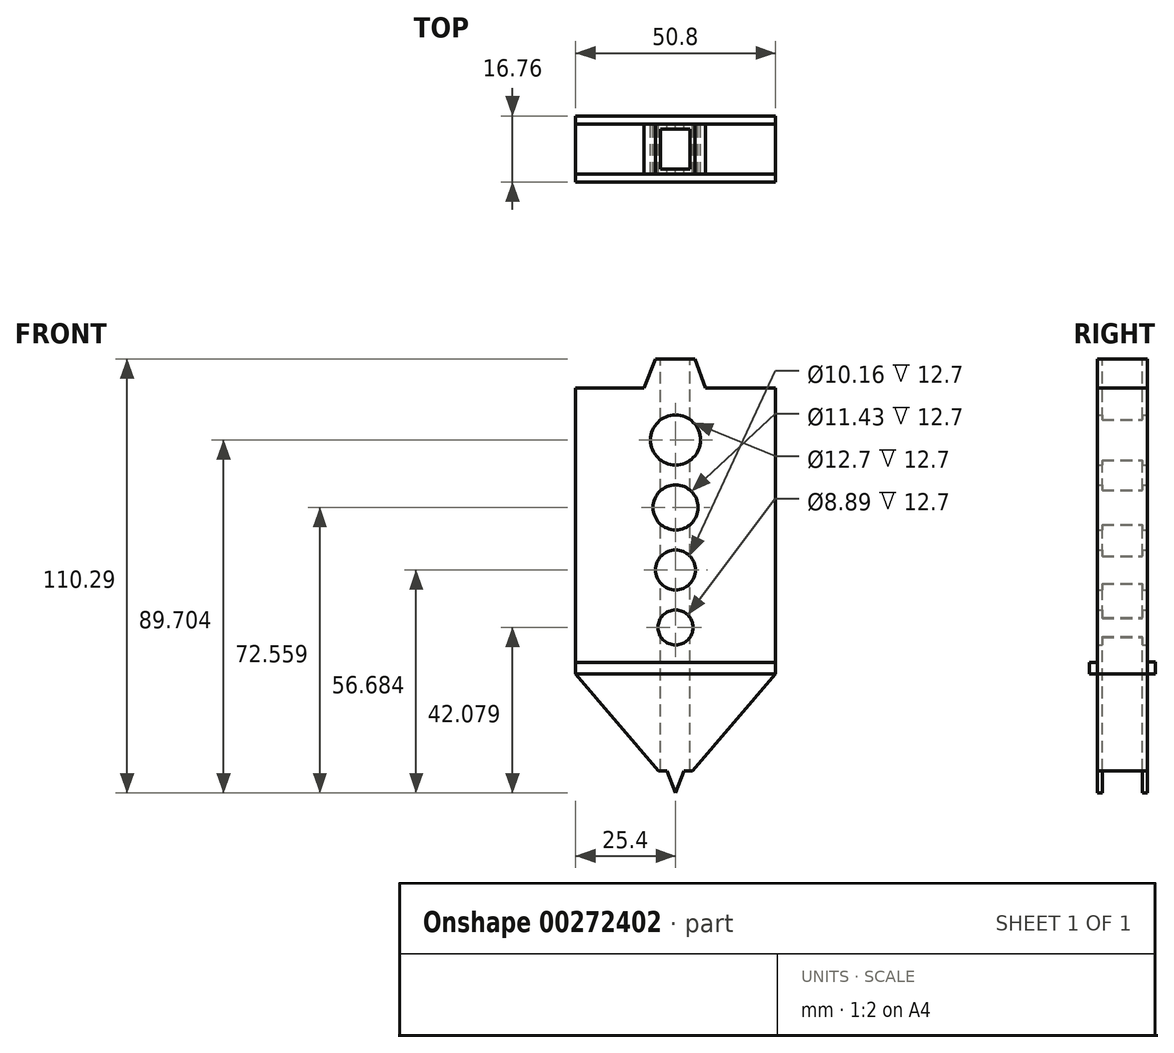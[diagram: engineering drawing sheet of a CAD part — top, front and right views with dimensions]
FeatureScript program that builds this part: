
annotation { "Feature Type Name" : "Feature", "Feature Type Description" : "" }
export const myFeature = defineFeature(function(context is Context, id is Id, definition is map)
    precondition{}
    {
        {
            var Q0;
            Q0=qCreatedBy(makeId("Front.planeOp"),FACE);
            var sketch = newSketch(context, id + "F0", { "sketchPlane" : qUnion([Q0])});
            skLineSegment(sketch, "E0", {"start": v(0, 0) * mm, "end": v(-25.4, 0) * mm});
            skLineSegment(sketch, "E1", {"start": v(0, 0) * mm, "end": v(25.4, 0) * mm});
            skLineSegment(sketch, "E2", {"start": v(-25.4, 0) * mm, "end": v(-4.32, -24.62) * mm});
            skLineSegment(sketch, "E3", {"start": v(-4.32, -24.62) * mm, "end": v(0, -24.62) * mm});
            skLineSegment(sketch, "E4", {"start": v(0, -24.62) * mm, "end": v(4.32, -24.62) * mm});
            skLineSegment(sketch, "E5", {"start": v(4.32, -24.62) * mm, "end": v(25.4, 0) * mm});
            skLineSegment(sketch, "E6", {"start": v(-2.16, -24.62) * mm, "end": v(0, -30.28) * mm});
            skLineSegment(sketch, "E7", {"start": v(0, -30.28) * mm, "end": v(2.16, -24.62) * mm});
            skLineSegment(sketch, "E8", {"start": v(-25.4, 0) * mm, "end": v(-25.4, 72.62) * mm});
            skLineSegment(sketch, "E9", {"start": v(-25.4, 72.62) * mm, "end": v(25.4, 72.62) * mm});
            skLineSegment(sketch, "E10", {"start": v(25.4, 72.62) * mm, "end": v(25.4, 0) * mm});
            skLineSegment(sketch, "E11", {"start": v(-8, 72.62) * mm, "end": v(-5.05, 80.01) * mm});
            skLineSegment(sketch, "E12", {"start": v(-5.05, 80.01) * mm, "end": v(4.91, 80.01) * mm});
            skLineSegment(sketch, "E13", {"start": v(4.91, 80.01) * mm, "end": v(7.55, 72.62) * mm});
            skLineSegment(sketch, "E14", {"start": v(0, 80.01) * mm, "end": v(-0.07, 72.62) * mm});
            skPoint(sketch, "E14.endSnap0", {"position": v(-0.07, 80.01) * mm});
            skCircle(sketch, "E15", {"center": v(0, 59.42) * mm, "radius": 6.35 * mm});
            skCircle(sketch, "E16", {"center": v(0, 42.28) * mm, "radius": 5.72 * mm});
            skCircle(sketch, "E17", {"center": v(0, 26.4) * mm, "radius": 5.08 * mm});
            skCircle(sketch, "E18", {"center": v(0, 11.8) * mm, "radius": 4.45 * mm});
            skSolve(sketch);
        }
        {
            var Q0;
            Q0=makeQuery(id+"F0.imprint","IMPRINT",FACE,{"disambiguationData":[TD([[makeQuery(id+"F0.imprint","IMPRINT",EDGE,{"derivedFrom":sQuery(id+"F0.wireOp",EDGE,"E0")}),-1.0]])]});
            var Q1;
            {var subQ0=sQuery(id+"F0.wireOp",EDGE,"E11");Q1=makeQuery(id+"F0.imprint","IMPRINT",FACE,{"disambiguationData":[TD([[makeQuery(id+"F0.imprint","IMPRINT",EDGE,{"derivedFrom":subQ0}),-1.0]])]});}
            var Q2;
            {var subQ0=sQuery(id+"F0.wireOp",EDGE,"E13");Q2=makeQuery(id+"F0.imprint","IMPRINT",FACE,{"disambiguationData":[TD([[makeQuery(id+"F0.imprint","IMPRINT",EDGE,{"derivedFrom":subQ0}),-1.0]])]});}
            var Q3;
            Q3=makeQuery(id+"F0.imprint","IMPRINT",FACE,{"disambiguationData":[TD([[makeQuery(id+"F0.imprint","IMPRINT",EDGE,{"derivedFrom":sQuery(id+"F0.wireOp",EDGE,"E0")}),1.0]])]});
            var Q4;
            {var subQ3=sQuery(id+"F0.wireOp",EDGE,"E6");Q4=makeQuery(id+"F0.imprint","IMPRINT",FACE,{"disambiguationData":[TD([[makeQuery(id+"F0.imprint","IMPRINT",EDGE,{"derivedFrom":subQ3}),1.0]])]});}
            extrude(context, id + "F1", {"entities" : qUnion([Q0, Q1, Q2, Q3, Q4]), "depth" : 12.7 * mm});
        }
        {
            var Q0;
            Q0=makeQuery(id+"F1.opExtrude","SWEPT_FACE",FACE,{"disambiguationData":[OSD([sQuery(id+"F0.wireOp",EDGE,"E12")])]});
            var sketch = newSketch(context, id + "F2", { "sketchPlane" : qUnion([Q0])});
            skLineSegment(sketch, "E19", {"start": v(-3.78, -1.27) * mm, "end": v(-3.78, -11.43) * mm});
            skLineSegment(sketch, "E20", {"start": v(-3.78, -11.43) * mm, "end": v(3.64, -11.43) * mm});
            skLineSegment(sketch, "E21", {"start": v(3.64, -11.43) * mm, "end": v(3.64, -1.27) * mm});
            skLineSegment(sketch, "E22", {"start": v(3.64, -1.27) * mm, "end": v(-3.78, -1.27) * mm});
            skSolve(sketch);
        }
        {
            var Q0;
            Q0 = qSketchRegion(id + "F2", true);
            extrude(context, id + "F3", {"entities" : qUnion([Q0]), "operationType" : NewBodyOperationType.REMOVE, "oppositeDirection" : true, "depth" : 127 * mm});
        }
        {
            var Q0;
            Q0=makeQuery(id+"F1.opExtrude","CAP_FACE",FACE,{"disambiguationData":[OSD([sQuery(id+"F0.wireOp",EDGE,"E2"),sQuery(id+"F0.wireOp",EDGE,"E3"),sQuery(id+"F0.wireOp",EDGE,"E4"),sQuery(id+"F0.wireOp",EDGE,"E5"),sQuery(id+"F0.wireOp",EDGE,"E6"),sQuery(id+"F0.wireOp",EDGE,"E7"),sQuery(id+"F0.wireOp",EDGE,"E8"),sQuery(id+"F0.wireOp",EDGE,"E9"),sQuery(id+"F0.wireOp",EDGE,"E10"),sQuery(id+"F0.wireOp",EDGE,"E11"),sQuery(id+"F0.wireOp",EDGE,"E12"),sQuery(id+"F0.wireOp",EDGE,"E13"),sQuery(id+"F0.wireOp",EDGE,"E15"),sQuery(id+"F0.wireOp",EDGE,"E16"),sQuery(id+"F0.wireOp",EDGE,"E17"),sQuery(id+"F0.wireOp",EDGE,"E18")])],"isStart":false});
            var sketch = newSketch(context, id + "F4", { "sketchPlane" : qUnion([Q0])});
            skLineSegment(sketch, "E23", {"start": v(0, 0) * mm, "end": v(-25.4, 0) * mm});
            skLineSegment(sketch, "E24", {"start": v(-25.4, 0) * mm, "end": v(25.4, 0) * mm});
            skLineSegment(sketch, "E25", {"start": v(0, 0) * mm, "end": v(0, 2.95) * mm});
            skLineSegment(sketch, "E26", {"start": v(0, 2.95) * mm, "end": v(-25.4, 2.95) * mm});
            skLineSegment(sketch, "E27", {"start": v(-25.4, 2.95) * mm, "end": v(25.4, 2.95) * mm});
            skSolve(sketch);
        }
        {
            var Q0;
            Q0 = qSketchRegion(id + "F4", true);
            var Q1;
            {var subQ3=sQuery(id+"F4.wireOp",EDGE,"E25");Q1=makeQuery(id+"F4.imprint","IMPRINT",FACE,{"disambiguationData":[TD([[makeQuery(id+"F4.imprint","IMPRINT",EDGE,{"derivedFrom":subQ3}),1.0]])]});}
            var Q2;
            {var subQ3=sQuery(id+"F4.wireOp",EDGE,"E25");Q2=makeQuery(id+"F4.imprint","IMPRINT",FACE,{"disambiguationData":[TD([[makeQuery(id+"F4.imprint","IMPRINT",EDGE,{"derivedFrom":subQ3}),-1.0]])]});}
            extrude(context, id + "F5", {"entities" : qUnion([Q0, Q1, Q2]), "depth" : 2.03 * mm});
        }
        {
            var Q0;
            Q0=makeQuery(id+"F1.opExtrude","CAP_FACE",FACE,{"disambiguationData":[OSD([sQuery(id+"F0.wireOp",EDGE,"E2"),sQuery(id+"F0.wireOp",EDGE,"E3"),sQuery(id+"F0.wireOp",EDGE,"E4"),sQuery(id+"F0.wireOp",EDGE,"E5"),sQuery(id+"F0.wireOp",EDGE,"E6"),sQuery(id+"F0.wireOp",EDGE,"E7"),sQuery(id+"F0.wireOp",EDGE,"E8"),sQuery(id+"F0.wireOp",EDGE,"E9"),sQuery(id+"F0.wireOp",EDGE,"E10"),sQuery(id+"F0.wireOp",EDGE,"E11"),sQuery(id+"F0.wireOp",EDGE,"E12"),sQuery(id+"F0.wireOp",EDGE,"E13"),sQuery(id+"F0.wireOp",EDGE,"E15"),sQuery(id+"F0.wireOp",EDGE,"E16"),sQuery(id+"F0.wireOp",EDGE,"E17"),sQuery(id+"F0.wireOp",EDGE,"E18")])],"isStart":true});
            var sketch = newSketch(context, id + "F6", { "sketchPlane" : qUnion([Q0])});
            skLineSegment(sketch, "E28", {"start": v(0, 0) * mm, "end": v(-25.4, 0) * mm});
            skLineSegment(sketch, "E29", {"start": v(-25.4, 0) * mm, "end": v(25.4, 0) * mm});
            skLineSegment(sketch, "E30", {"start": v(0, 0) * mm, "end": v(0, 3.05) * mm});
            skLineSegment(sketch, "E31", {"start": v(0, 3.05) * mm, "end": v(-25.4, 3.05) * mm});
            skLineSegment(sketch, "E32", {"start": v(-25.4, 3.05) * mm, "end": v(25.4, 3.05) * mm});
            skSolve(sketch);
        }
        {
            var Q0;
            {var subQ3=sQuery(id+"F6.wireOp",EDGE,"E30");Q0=makeQuery(id+"F6.imprint","IMPRINT",FACE,{"disambiguationData":[TD([[makeQuery(id+"F6.imprint","IMPRINT",EDGE,{"derivedFrom":subQ3}),1.0]])]});}
            var Q1;
            {var subQ3=sQuery(id+"F6.wireOp",EDGE,"E30");Q1=makeQuery(id+"F6.imprint","IMPRINT",FACE,{"disambiguationData":[TD([[makeQuery(id+"F6.imprint","IMPRINT",EDGE,{"derivedFrom":subQ3}),-1.0]])]});}
            extrude(context, id + "F7", {"entities" : qUnion([Q0, Q1]), "depth" : 2.03 * mm});
        }
    });
